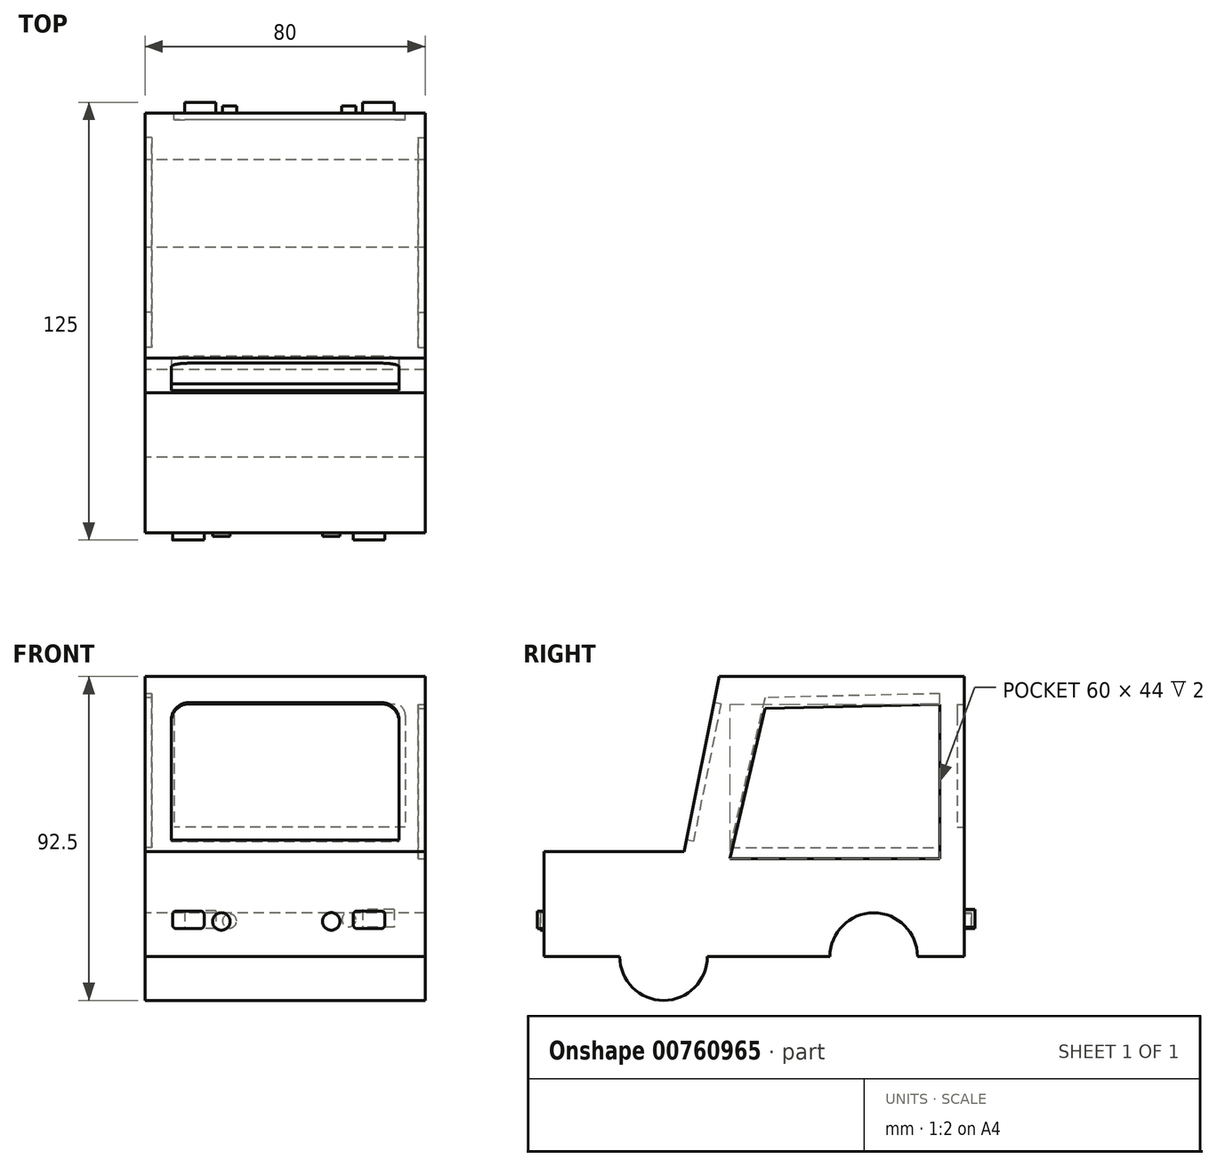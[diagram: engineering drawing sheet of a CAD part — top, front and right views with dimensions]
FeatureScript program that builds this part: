
annotation { "Feature Type Name" : "Feature", "Feature Type Description" : "" }
export const myFeature = defineFeature(function(context is Context, id is Id, definition is map)
    precondition{}
    {
        {
            var Q0;
            Q0=qCreatedBy(makeId("Right.planeOp"),FACE);
            var sketch = newSketch(context, id + "F0", { "sketchPlane" : qUnion([Q0])});
            skLineSegment(sketch, "E0", {"start": v(56.98, 39.53) * mm, "end": v(56.98, -40.47) * mm});
            skLineSegment(sketch, "E1", {"start": v(56.98, 39.53) * mm, "end": v(-13.02, 39.53) * mm});
            skLineSegment(sketch, "E2", {"start": v(56.98, -40.47) * mm, "end": v(-63.02, -40.47) * mm});
            skLineSegment(sketch, "E3", {"start": v(-63.02, -40.47) * mm, "end": v(-63.02, -10.47) * mm});
            skLineSegment(sketch, "E4", {"start": v(-63.02, -10.47) * mm, "end": v(-23.02, -10.47) * mm});
            skLineSegment(sketch, "E5", {"start": v(-23.02, -10.47) * mm, "end": v(-13.02, 39.53) * mm});
            skCircle(sketch, "E6", {"center": v(-28.91, -40.47) * mm, "radius": 12.5 * mm});
            skCircle(sketch, "E7", {"center": v(31.09, -40.47) * mm, "radius": 12.5 * mm});
            skSolve(sketch);
        }
        {
            var Q0;
            {var subQ5=sQuery(id+"F0.wireOp",EDGE,"E0");Q0=makeQuery(id+"F0.imprint","IMPRINT",FACE,{"disambiguationData":[TD([[makeQuery(id+"F0.imprint","IMPRINT",EDGE,{"derivedFrom":subQ5}),-1.0]])]});}
            var Q1;
            {var subQ0=sQuery(id+"F0.wireOp",EDGE,"E6");var subQ1=sQuery(id+"F0.wireOp",EDGE,"E2");var subQ2=makeQuery(id+"F0.imprint","INTERSECT",VERTEX,{"disambiguationData":[OD(0.0)],"derivedFrom":[subQ1,subQ0]});Q1=makeQuery(id+"F0.imprint","IMPRINT",FACE,{"disambiguationData":[TD([[makeQuery(id+"F0.imprint","IMPRINT",EDGE,{"disambiguationData":[TD([[subQ2,-1.0]])],"derivedFrom":subQ1}),-1.0]])]});}
            var Q2;
            {var subQ0=sQuery(id+"F0.wireOp",EDGE,"E6");var subQ1=sQuery(id+"F0.wireOp",EDGE,"E2");var subQ2=makeQuery(id+"F0.imprint","INTERSECT",VERTEX,{"disambiguationData":[OD(0.0)],"derivedFrom":[subQ1,subQ0]});Q2=makeQuery(id+"F0.imprint","IMPRINT",FACE,{"disambiguationData":[TD([[makeQuery(id+"F0.imprint","IMPRINT",EDGE,{"disambiguationData":[TD([[subQ2,-1.0]])],"derivedFrom":subQ1}),1.0]])]});}
            var Q3;
            {var subQ0=sQuery(id+"F0.wireOp",EDGE,"E7");var subQ1=sQuery(id+"F0.wireOp",EDGE,"E2");var subQ2=makeQuery(id+"F0.imprint","INTERSECT",VERTEX,{"disambiguationData":[OD(0.0)],"derivedFrom":[subQ1,subQ0]});Q3=makeQuery(id+"F0.imprint","IMPRINT",FACE,{"disambiguationData":[TD([[makeQuery(id+"F0.imprint","IMPRINT",EDGE,{"disambiguationData":[TD([[subQ2,-1.0]])],"derivedFrom":subQ1}),1.0]])]});}
            var Q4;
            {var subQ0=sQuery(id+"F0.wireOp",EDGE,"E7");var subQ1=sQuery(id+"F0.wireOp",EDGE,"E2");var subQ2=makeQuery(id+"F0.imprint","INTERSECT",VERTEX,{"disambiguationData":[OD(0.0)],"derivedFrom":[subQ1,subQ0]});Q4=makeQuery(id+"F0.imprint","IMPRINT",FACE,{"disambiguationData":[TD([[makeQuery(id+"F0.imprint","IMPRINT",EDGE,{"disambiguationData":[TD([[subQ2,-1.0]])],"derivedFrom":subQ1}),-1.0]])]});}
            extrude(context, id + "F1", {"entities" : qUnion([Q0, Q1, Q2, Q3, Q4]), "depth" : 80 * mm, "offsetDistance" : 25 * mm});
        }
        {
            var Q0;
            Q0=makeQuery(id+"F1.opExtrude","CAP_FACE",FACE,{"disambiguationData":[OSD([sQuery(id+"F0.wireOp",EDGE,"E0"),sQuery(id+"F0.wireOp",EDGE,"E1"),sQuery(id+"F0.wireOp",EDGE,"E2"),sQuery(id+"F0.wireOp",EDGE,"E3"),sQuery(id+"F0.wireOp",EDGE,"E4"),sQuery(id+"F0.wireOp",EDGE,"E5"),sQuery(id+"F0.wireOp",EDGE,"E6"),sQuery(id+"F0.wireOp",EDGE,"E7")])],"isStart":false});
            var sketch = newSketch(context, id + "F2", { "sketchPlane" : qUnion([Q0])});
            skLineSegment(sketch, "E8", {"start": v(0, 30.37) * mm, "end": v(-10.01, -12.47) * mm});
            skLineSegment(sketch, "E9", {"start": v(-10.01, -12.47) * mm, "end": v(49.99, -12.47) * mm});
            skLineSegment(sketch, "E10", {"start": v(49.99, -12.47) * mm, "end": v(49.99, 31.53) * mm});
            skLineSegment(sketch, "E11", {"start": v(49.99, 31.53) * mm, "end": v(0, 30.37) * mm});
            skSolve(sketch);
        }
        {
            var Q0;
            Q0 = qSketchRegion(id + "F2", true);
            extrude(context, id + "F3", {"entities" : qUnion([Q0]), "operationType" : NewBodyOperationType.REMOVE, "oppositeDirection" : true, "depth" : 2 * mm, "offsetDistance" : 25 * mm});
        }
        {
            var Q0;
            Q0=makeQuery(id+"F1.opExtrude","CAP_FACE",FACE,{"disambiguationData":[OSD([sQuery(id+"F0.wireOp",EDGE,"E0"),sQuery(id+"F0.wireOp",EDGE,"E1"),sQuery(id+"F0.wireOp",EDGE,"E2"),sQuery(id+"F0.wireOp",EDGE,"E3"),sQuery(id+"F0.wireOp",EDGE,"E4"),sQuery(id+"F0.wireOp",EDGE,"E5"),sQuery(id+"F0.wireOp",EDGE,"E6"),sQuery(id+"F0.wireOp",EDGE,"E7")])],"isStart":true});
            var sketch = newSketch(context, id + "F4", { "sketchPlane" : qUnion([Q0])});
            skLineSegment(sketch, "E12", {"start": v(0, 33.48) * mm, "end": v(10.01, -9.36) * mm});
            skLineSegment(sketch, "E13", {"start": v(10.01, -9.36) * mm, "end": v(-49.99, -9.36) * mm});
            skLineSegment(sketch, "E14", {"start": v(-49.99, -9.36) * mm, "end": v(-49.99, 34.64) * mm});
            skLineSegment(sketch, "E15", {"start": v(-49.99, 34.64) * mm, "end": v(0, 33.48) * mm});
            skSolve(sketch);
        }
        {
            var Q0;
            Q0=makeQuery(id+"F4.imprint","IMPRINT",FACE,{"disambiguationData":[TD([[makeQuery(id+"F4.imprint","IMPRINT",EDGE,{"derivedFrom":sQuery(id+"F4.wireOp",EDGE,"E12")}),-1.0]])]});
            extrude(context, id + "F5", {"entities" : qUnion([Q0]), "operationType" : NewBodyOperationType.REMOVE, "oppositeDirection" : true, "depth" : 2 * mm, "offsetDistance" : 25 * mm});
        }
        {
            var Q0;
            Q0=makeQuery(id+"F1.opExtrude","SWEPT_FACE",FACE,{"disambiguationData":[OSD([sQuery(id+"F0.wireOp",EDGE,"E5")])]});
            var sketch = newSketch(context, id + "F6", { "sketchPlane" : qUnion([Q0])});
            skLineSegment(sketch, "E16", {"start": v(7.54, 23.62) * mm, "end": v(7.54, -11.38) * mm});
            skLineSegment(sketch, "E17", {"start": v(7.54, -11.38) * mm, "end": v(72.54, -11.38) * mm});
            skLineSegment(sketch, "E18", {"start": v(72.54, -11.38) * mm, "end": v(72.54, 23.62) * mm});
            skLineSegment(sketch, "E19", {"start": v(67.54, 28.62) * mm, "end": v(12.54, 28.62) * mm});
            skPoint(sketch, "E20.visualSharp", {"position": v(7.54, 28.62) * mm});
            skArc(sketch, "E20.filletArc", {"start": v(12.54, 28.62) * mm, "mid": v(9, 27.15) * mm, "end": v(7.54, 23.62) * mm});
            skPoint(sketch, "E21.visualSharp", {"position": v(72.54, 28.62) * mm});
            skArc(sketch, "E21.filletArc", {"start": v(72.54, 23.62) * mm, "mid": v(71.08, 27.15) * mm, "end": v(67.54, 28.62) * mm});
            skSolve(sketch);
        }
        {
            var Q0;
            Q0=makeQuery(id+"F6.imprint","IMPRINT",FACE,{"disambiguationData":[TD([[makeQuery(id+"F6.imprint","IMPRINT",EDGE,{"derivedFrom":sQuery(id+"F6.wireOp",EDGE,"E16")}),1.0]])]});
            extrude(context, id + "F7", {"entities" : qUnion([Q0]), "operationType" : NewBodyOperationType.REMOVE, "oppositeDirection" : true, "depth" : 2 * mm, "offsetDistance" : 25 * mm});
        }
        {
            var Q0;
            Q0=makeQuery(id+"F1.opExtrude","SWEPT_FACE",FACE,{"disambiguationData":[OSD([sQuery(id+"F0.wireOp",EDGE,"E3")])]});
            var sketch = newSketch(context, id + "F8", { "sketchPlane" : qUnion([Q0])});
            skLineSegment(sketch, "E22.bottom", {"start": v(15.88, -27.45) * mm, "end": v(8.88, -27.45) * mm});
            skLineSegment(sketch, "E22.top", {"start": v(15.88, -32.45) * mm, "end": v(8.88, -32.45) * mm});
            skLineSegment(sketch, "E22.left", {"start": v(16.88, -28.45) * mm, "end": v(16.88, -31.45) * mm});
            skLineSegment(sketch, "E22.right", {"start": v(7.88, -28.45) * mm, "end": v(7.88, -31.45) * mm});
            skPoint(sketch, "E22.middle", {"position": v(12.38, -29.95) * mm});
            skLineSegment(sketch, "E23.bottom", {"start": v(67.5, -27.45) * mm, "end": v(60.5, -27.45) * mm});
            skLineSegment(sketch, "E23.top", {"start": v(67.5, -32.45) * mm, "end": v(60.5, -32.45) * mm});
            skLineSegment(sketch, "E23.left", {"start": v(68.5, -28.45) * mm, "end": v(68.5, -31.45) * mm});
            skLineSegment(sketch, "E23.right", {"start": v(59.5, -28.45) * mm, "end": v(59.5, -31.45) * mm});
            skPoint(sketch, "E23.middle", {"position": v(64, -29.95) * mm});
            skPoint(sketch, "E24.visualSharp", {"position": v(7.88, -27.45) * mm});
            skArc(sketch, "E24.filletArc", {"start": v(8.88, -27.45) * mm, "mid": v(8.17, -27.74) * mm, "end": v(7.88, -28.45) * mm});
            skPoint(sketch, "E25.visualSharp", {"position": v(16.88, -27.45) * mm});
            skArc(sketch, "E25.filletArc", {"start": v(16.88, -28.45) * mm, "mid": v(16.59, -27.74) * mm, "end": v(15.88, -27.45) * mm});
            skPoint(sketch, "E26.visualSharp", {"position": v(16.88, -32.45) * mm});
            skArc(sketch, "E26.filletArc", {"start": v(15.88, -32.45) * mm, "mid": v(16.59, -32.15) * mm, "end": v(16.88, -31.45) * mm});
            skPoint(sketch, "E27.visualSharp", {"position": v(7.88, -32.45) * mm});
            skArc(sketch, "E27.filletArc", {"start": v(7.88, -31.45) * mm, "mid": v(8.17, -32.15) * mm, "end": v(8.88, -32.45) * mm});
            skPoint(sketch, "E28.visualSharp", {"position": v(68.5, -27.45) * mm});
            skArc(sketch, "E28.filletArc", {"start": v(68.5, -28.45) * mm, "mid": v(68.22, -27.74) * mm, "end": v(67.5, -27.45) * mm});
            skPoint(sketch, "E29.visualSharp", {"position": v(59.5, -27.45) * mm});
            skArc(sketch, "E29.filletArc", {"start": v(60.5, -27.45) * mm, "mid": v(59.8, -27.74) * mm, "end": v(59.5, -28.45) * mm});
            skPoint(sketch, "E30.visualSharp", {"position": v(59.5, -32.45) * mm});
            skArc(sketch, "E30.filletArc", {"start": v(59.5, -31.45) * mm, "mid": v(59.8, -32.15) * mm, "end": v(60.5, -32.45) * mm});
            skPoint(sketch, "E31.visualSharp", {"position": v(68.5, -32.45) * mm});
            skArc(sketch, "E31.filletArc", {"start": v(67.5, -32.45) * mm, "mid": v(68.22, -32.15) * mm, "end": v(68.5, -31.45) * mm});
            skSolve(sketch);
        }
        {
            var Q0;
            Q0=makeQuery(id+"F8.imprint","IMPRINT",FACE,{"disambiguationData":[TD([[makeQuery(id+"F8.imprint","IMPRINT",EDGE,{"derivedFrom":sQuery(id+"F8.wireOp",EDGE,"E22.bottom")}),1.0]])]});
            var Q1;
            Q1=makeQuery(id+"F8.imprint","IMPRINT",FACE,{"disambiguationData":[TD([[makeQuery(id+"F8.imprint","IMPRINT",EDGE,{"derivedFrom":sQuery(id+"F8.wireOp",EDGE,"E23.bottom")}),1.0]])]});
            extrude(context, id + "F9", {"entities" : qUnion([Q0, Q1]), "operationType" : NewBodyOperationType.ADD, "depth" : 2 * mm, "offsetDistance" : 25 * mm});
        }
        {
            var Q0;
            Q0=makeQuery(id+"F1.opExtrude","SWEPT_FACE",FACE,{"disambiguationData":[OSD([sQuery(id+"F0.wireOp",EDGE,"E3")])]});
            var sketch = newSketch(context, id + "F10", { "sketchPlane" : qUnion([Q0])});
            skCircle(sketch, "E32", {"center": v(21.82, -30.44) * mm, "radius": 2.5 * mm});
            skCircle(sketch, "E33", {"center": v(53.2, -30.42) * mm, "radius": 2.5 * mm});
            skSolve(sketch);
        }
        {
            var Q0;
            Q0=makeQuery(id+"F10.imprint","IMPRINT",FACE,{"disambiguationData":[TD([[makeQuery(id+"F10.imprint","IMPRINT",EDGE,{"derivedFrom":sQuery(id+"F10.wireOp",EDGE,"E32")}),1.0]])]});
            var Q1;
            Q1=makeQuery(id+"F10.imprint","IMPRINT",FACE,{"disambiguationData":[TD([[makeQuery(id+"F10.imprint","IMPRINT",EDGE,{"derivedFrom":sQuery(id+"F10.wireOp",EDGE,"E33")}),1.0]])]});
            extrude(context, id + "F11", {"entities" : qUnion([Q0, Q1]), "operationType" : NewBodyOperationType.ADD, "depth" : 1 * mm, "offsetDistance" : 25 * mm});
        }
        {
            var Q0;
            Q0=makeQuery(id+"F1.opExtrude","SWEPT_FACE",FACE,{"disambiguationData":[OSD([sQuery(id+"F0.wireOp",EDGE,"E0")])]});
            var sketch = newSketch(context, id + "F12", { "sketchPlane" : qUnion([Q0])});
            skLineSegment(sketch, "E34.bottom", {"start": v(-71.35, 31.54) * mm, "end": v(-11.35, 31.54) * mm});
            skLineSegment(sketch, "E34.top", {"start": v(-74.35, -3.46) * mm, "end": v(-8.35, -3.46) * mm});
            skLineSegment(sketch, "E34.left", {"start": v(-74.35, 28.54) * mm, "end": v(-74.35, -3.46) * mm});
            skLineSegment(sketch, "E34.right", {"start": v(-8.35, 28.54) * mm, "end": v(-8.35, -3.46) * mm});
            skPoint(sketch, "E35.visualSharp", {"position": v(-74.35, 31.54) * mm});
            skArc(sketch, "E35.filletArc", {"start": v(-71.35, 31.54) * mm, "mid": v(-73.47, 30.67) * mm, "end": v(-74.35, 28.54) * mm});
            skPoint(sketch, "E36.visualSharp", {"position": v(-8.35, 31.54) * mm});
            skArc(sketch, "E36.filletArc", {"start": v(-8.35, 28.54) * mm, "mid": v(-9.23, 30.67) * mm, "end": v(-11.35, 31.54) * mm});
            skSolve(sketch);
        }
        {
            var Q0;
            Q0=makeQuery(id+"F12.imprint","IMPRINT",FACE,{"disambiguationData":[TD([[makeQuery(id+"F12.imprint","IMPRINT",EDGE,{"derivedFrom":sQuery(id+"F12.wireOp",EDGE,"E34.bottom")}),-1.0]])]});
            extrude(context, id + "F13", {"entities" : qUnion([Q0]), "operationType" : NewBodyOperationType.REMOVE, "oppositeDirection" : true, "depth" : 2 * mm, "offsetDistance" : 25 * mm});
        }
        {
            var Q0;
            Q0=makeQuery(id+"F1.opExtrude","SWEPT_FACE",FACE,{"disambiguationData":[OSD([sQuery(id+"F0.wireOp",EDGE,"E0")])]});
            var sketch = newSketch(context, id + "F14", { "sketchPlane" : qUnion([Q0])});
            skLineSegment(sketch, "E37.bottom", {"start": v(-71.12, -27.03) * mm, "end": v(-62.12, -27.03) * mm});
            skLineSegment(sketch, "E37.top", {"start": v(-71.12, -32.03) * mm, "end": v(-62.12, -32.03) * mm});
            skLineSegment(sketch, "E37.left", {"start": v(-71.12, -27.03) * mm, "end": v(-71.12, -32.03) * mm});
            skLineSegment(sketch, "E37.right", {"start": v(-62.12, -27.03) * mm, "end": v(-62.12, -32.03) * mm});
            skLineSegment(sketch, "E38.bottom", {"start": v(-20.3, -27.39) * mm, "end": v(-11.3, -27.39) * mm});
            skLineSegment(sketch, "E38.top", {"start": v(-20.3, -32.39) * mm, "end": v(-11.3, -32.39) * mm});
            skLineSegment(sketch, "E38.left", {"start": v(-20.3, -27.39) * mm, "end": v(-20.3, -32.39) * mm});
            skLineSegment(sketch, "E38.right", {"start": v(-11.3, -27.39) * mm, "end": v(-11.3, -32.39) * mm});
            skSolve(sketch);
        }
        {
            var Q0;
            Q0=makeQuery(id+"F14.imprint","IMPRINT",FACE,{"disambiguationData":[TD([[makeQuery(id+"F14.imprint","IMPRINT",EDGE,{"derivedFrom":sQuery(id+"F14.wireOp",EDGE,"E37.bottom")}),-1.0]])]});
            var Q1;
            Q1=makeQuery(id+"F14.imprint","IMPRINT",FACE,{"disambiguationData":[TD([[makeQuery(id+"F14.imprint","IMPRINT",EDGE,{"derivedFrom":sQuery(id+"F14.wireOp",EDGE,"E38.bottom")}),-1.0]])]});
            extrude(context, id + "F15", {"entities" : qUnion([Q0, Q1]), "operationType" : NewBodyOperationType.ADD, "depth" : 3 * mm, "offsetDistance" : 25 * mm});
        }
        {
            var Q0;
            Q0=makeQuery(id+"F1.opExtrude","SWEPT_FACE",FACE,{"disambiguationData":[OSD([sQuery(id+"F0.wireOp",EDGE,"E0")])]});
            var sketch = newSketch(context, id + "F16", { "sketchPlane" : qUnion([Q0])});
            skCircle(sketch, "E39", {"center": v(-58.24, -29.94) * mm, "radius": 2 * mm});
            skCircle(sketch, "E40", {"center": v(-24.15, -30.32) * mm, "radius": 2 * mm});
            skSolve(sketch);
        }
        {
            var Q0;
            Q0=makeQuery(id+"F16.imprint","IMPRINT",FACE,{"disambiguationData":[TD([[makeQuery(id+"F16.imprint","IMPRINT",EDGE,{"derivedFrom":sQuery(id+"F16.wireOp",EDGE,"E40")}),1.0]])]});
            var Q1;
            Q1=makeQuery(id+"F16.imprint","IMPRINT",FACE,{"disambiguationData":[TD([[makeQuery(id+"F16.imprint","IMPRINT",EDGE,{"derivedFrom":sQuery(id+"F16.wireOp",EDGE,"E39")}),1.0]])]});
            extrude(context, id + "F17", {"entities" : qUnion([Q0, Q1]), "operationType" : NewBodyOperationType.ADD, "depth" : 2 * mm, "offsetDistance" : 25 * mm});
        }
    });
